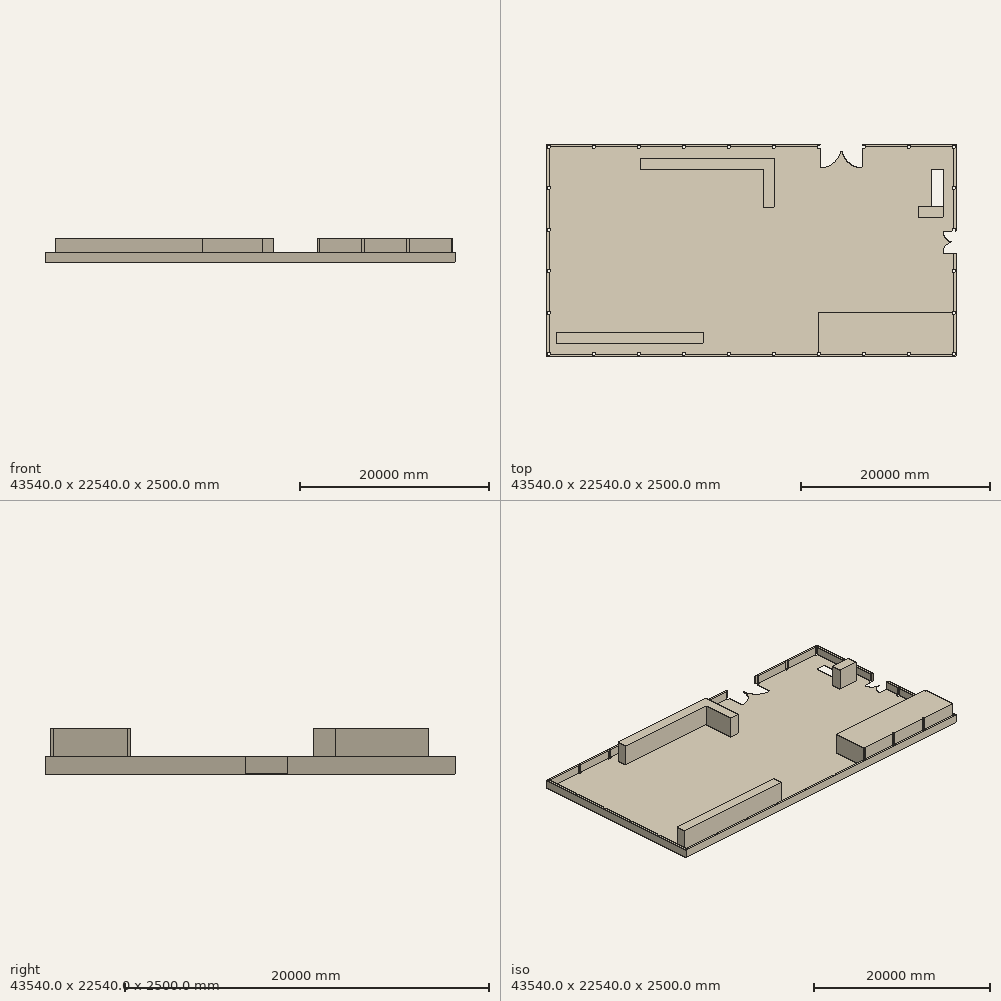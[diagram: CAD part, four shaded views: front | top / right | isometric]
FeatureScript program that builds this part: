
annotation { "Feature Type Name" : "Feature", "Feature Type Description" : "" }
export const myFeature = defineFeature(function(context is Context, id is Id, definition is map)
    precondition{}
    {
        {
            var Q0;
            Q0=qCreatedBy(makeId("Top.planeOp"),FACE);
            var sketch = newSketch(context, id + "F0", { "sketchPlane" : qUnion([Q0])});
            skLineSegment(sketch, "E0", {"start": v(0, 22000) * mm, "end": v(43000, 22000) * mm});
            skLineSegment(sketch, "E1", {"start": v(43000, 22000) * mm, "end": v(43000, 4400) * mm});
            skLineSegment(sketch, "E2", {"start": v(0, 22000) * mm, "end": v(0, 0) * mm});
            skLineSegment(sketch, "E3", {"start": v(0, 0) * mm, "end": v(28666.67, 0) * mm});
            skLineSegment(sketch, "E4.bottom", {"start": v(170, 22170) * mm, "end": v(-170, 22170) * mm});
            skLineSegment(sketch, "E4.top", {"start": v(170, 21830) * mm, "end": v(-170, 21830) * mm});
            skLineSegment(sketch, "E4.left", {"start": v(170, 22170) * mm, "end": v(170, 21830) * mm});
            skLineSegment(sketch, "E4.right", {"start": v(-170, 22170) * mm, "end": v(-170, 21830) * mm});
            skPoint(sketch, "E4.middle", {"position": v(0, 22000) * mm});
            skLineSegment(sketch, "E5.bottom", {"start": v(170, 170) * mm, "end": v(-170, 170) * mm});
            skLineSegment(sketch, "E5.top", {"start": v(170, -170) * mm, "end": v(-170, -170) * mm});
            skLineSegment(sketch, "E5.left", {"start": v(170, 170) * mm, "end": v(170, -170) * mm});
            skLineSegment(sketch, "E5.right", {"start": v(-170, 170) * mm, "end": v(-170, -170) * mm});
            skPoint(sketch, "E5.middle", {"position": v(0, 0) * mm});
            skLineSegment(sketch, "E6.0.1.0", {"start": v(170, 4230) * mm, "end": v(-170, 4230) * mm});
            skLineSegment(sketch, "E6.0.1.1", {"start": v(170, 4570) * mm, "end": v(-170, 4570) * mm});
            skLineSegment(sketch, "E6.0.1.2", {"start": v(170, 4570) * mm, "end": v(170, 4230) * mm});
            skLineSegment(sketch, "E6.0.1.3", {"start": v(-170, 4570) * mm, "end": v(-170, 4230) * mm});
            skLineSegment(sketch, "E6.0.2.0", {"start": v(170, 8630) * mm, "end": v(-170, 8630) * mm});
            skLineSegment(sketch, "E6.0.2.1", {"start": v(170, 8970) * mm, "end": v(-170, 8970) * mm});
            skLineSegment(sketch, "E6.0.2.2", {"start": v(170, 8970) * mm, "end": v(170, 8630) * mm});
            skLineSegment(sketch, "E6.0.2.3", {"start": v(-170, 8970) * mm, "end": v(-170, 8630) * mm});
            skLineSegment(sketch, "E6.0.3.0", {"start": v(170, 13030) * mm, "end": v(-170, 13030) * mm});
            skLineSegment(sketch, "E6.0.3.1", {"start": v(170, 13370) * mm, "end": v(-170, 13370) * mm});
            skLineSegment(sketch, "E6.0.3.2", {"start": v(170, 13370) * mm, "end": v(170, 13030) * mm});
            skLineSegment(sketch, "E6.0.3.3", {"start": v(-170, 13370) * mm, "end": v(-170, 13030) * mm});
            skLineSegment(sketch, "E6.0.4.0", {"start": v(170, 17430) * mm, "end": v(-170, 17430) * mm});
            skLineSegment(sketch, "E6.0.4.1", {"start": v(170, 17770) * mm, "end": v(-170, 17770) * mm});
            skLineSegment(sketch, "E6.0.4.2", {"start": v(170, 17770) * mm, "end": v(170, 17430) * mm});
            skLineSegment(sketch, "E6.0.4.3", {"start": v(-170, 17770) * mm, "end": v(-170, 17430) * mm});
            skLineSegment(sketch, "E7.0.1.0", {"start": v(43170, 4570) * mm, "end": v(43170, 4230) * mm});
            skPoint(sketch, "E7.0.1.1", {"position": v(43000, 4400) * mm});
            skLineSegment(sketch, "E7.0.1.2", {"start": v(42830, 4570) * mm, "end": v(42830, 4230) * mm});
            skLineSegment(sketch, "E7.0.1.4", {"start": v(43170, 4230) * mm, "end": v(42830, 4230) * mm});
            skLineSegment(sketch, "E7.0.1.5", {"start": v(43170, 4570) * mm, "end": v(42830, 4570) * mm});
            skLineSegment(sketch, "E7.0.2.0", {"start": v(43170, 8970) * mm, "end": v(43170, 8630) * mm});
            skPoint(sketch, "E7.0.2.1", {"position": v(43000, 8800) * mm});
            skLineSegment(sketch, "E7.0.2.2", {"start": v(42830, 8970) * mm, "end": v(42830, 8630) * mm});
            skLineSegment(sketch, "E7.0.2.4", {"start": v(43170, 8630) * mm, "end": v(42830, 8630) * mm});
            skLineSegment(sketch, "E7.0.2.5", {"start": v(43170, 8970) * mm, "end": v(42830, 8970) * mm});
            skLineSegment(sketch, "E7.0.3.0", {"start": v(43170, 13370) * mm, "end": v(43170, 13030) * mm});
            skPoint(sketch, "E7.0.3.1", {"position": v(43000, 13200) * mm});
            skLineSegment(sketch, "E7.0.3.2", {"start": v(42830, 13370) * mm, "end": v(42830, 13030) * mm});
            skLineSegment(sketch, "E7.0.3.4", {"start": v(43170, 13030) * mm, "end": v(42830, 13030) * mm});
            skLineSegment(sketch, "E7.0.3.5", {"start": v(43170, 13370) * mm, "end": v(42830, 13370) * mm});
            skLineSegment(sketch, "E7.0.4.0", {"start": v(43170, 17770) * mm, "end": v(43170, 17430) * mm});
            skPoint(sketch, "E7.0.4.1", {"position": v(43000, 17600) * mm});
            skLineSegment(sketch, "E7.0.4.2", {"start": v(42830, 17770) * mm, "end": v(42830, 17430) * mm});
            skLineSegment(sketch, "E7.0.4.4", {"start": v(43170, 17430) * mm, "end": v(42830, 17430) * mm});
            skLineSegment(sketch, "E7.0.4.5", {"start": v(43170, 17770) * mm, "end": v(42830, 17770) * mm});
            skPoint(sketch, "E8.1.0.0", {"position": v(4777.78, 22000) * mm});
            skLineSegment(sketch, "E8.1.0.1", {"start": v(4947.78, 22170) * mm, "end": v(4607.78, 22170) * mm});
            skLineSegment(sketch, "E8.1.0.2", {"start": v(4947.78, 22170) * mm, "end": v(4947.78, 21830) * mm});
            skLineSegment(sketch, "E8.1.0.3", {"start": v(4607.78, 22170) * mm, "end": v(4607.78, 21830) * mm});
            skLineSegment(sketch, "E8.1.0.4", {"start": v(4947.78, 21830) * mm, "end": v(4607.78, 21830) * mm});
            skPoint(sketch, "E8.2.0.0", {"position": v(9555.56, 22000) * mm});
            skLineSegment(sketch, "E8.2.0.1", {"start": v(9725.56, 22170) * mm, "end": v(9385.56, 22170) * mm});
            skLineSegment(sketch, "E8.2.0.2", {"start": v(9725.56, 22170) * mm, "end": v(9725.56, 21830) * mm});
            skLineSegment(sketch, "E8.2.0.3", {"start": v(9385.56, 22170) * mm, "end": v(9385.56, 21830) * mm});
            skLineSegment(sketch, "E8.2.0.4", {"start": v(9725.56, 21830) * mm, "end": v(9385.56, 21830) * mm});
            skPoint(sketch, "E8.3.0.0", {"position": v(14333.33, 22000) * mm});
            skLineSegment(sketch, "E8.3.0.1", {"start": v(14503.33, 22170) * mm, "end": v(14163.33, 22170) * mm});
            skLineSegment(sketch, "E8.3.0.2", {"start": v(14503.33, 22170) * mm, "end": v(14503.33, 21830) * mm});
            skLineSegment(sketch, "E8.3.0.3", {"start": v(14163.33, 22170) * mm, "end": v(14163.33, 21830) * mm});
            skLineSegment(sketch, "E8.3.0.4", {"start": v(14503.33, 21830) * mm, "end": v(14163.33, 21830) * mm});
            skPoint(sketch, "E8.4.0.0", {"position": v(19111.11, 22000) * mm});
            skLineSegment(sketch, "E8.4.0.1", {"start": v(19281.11, 22170) * mm, "end": v(18941.11, 22170) * mm});
            skLineSegment(sketch, "E8.4.0.2", {"start": v(19281.11, 22170) * mm, "end": v(19281.11, 21830) * mm});
            skLineSegment(sketch, "E8.4.0.3", {"start": v(18941.11, 22170) * mm, "end": v(18941.11, 21830) * mm});
            skLineSegment(sketch, "E8.4.0.4", {"start": v(19281.11, 21830) * mm, "end": v(18941.11, 21830) * mm});
            skPoint(sketch, "E8.5.0.0", {"position": v(23888.89, 22000) * mm});
            skLineSegment(sketch, "E8.5.0.1", {"start": v(24058.89, 22170) * mm, "end": v(23718.89, 22170) * mm});
            skLineSegment(sketch, "E8.5.0.2", {"start": v(24058.89, 22170) * mm, "end": v(24058.89, 21830) * mm});
            skLineSegment(sketch, "E8.5.0.3", {"start": v(23718.89, 22170) * mm, "end": v(23718.89, 21830) * mm});
            skLineSegment(sketch, "E8.5.0.4", {"start": v(24058.89, 21830) * mm, "end": v(23718.89, 21830) * mm});
            skPoint(sketch, "E8.6.0.0", {"position": v(28666.67, 22000) * mm});
            skLineSegment(sketch, "E8.6.0.1", {"start": v(28836.67, 22170) * mm, "end": v(28496.67, 22170) * mm});
            skLineSegment(sketch, "E8.6.0.2", {"start": v(28836.67, 22170) * mm, "end": v(28836.67, 21830) * mm});
            skLineSegment(sketch, "E8.6.0.3", {"start": v(28496.67, 22170) * mm, "end": v(28496.67, 21830) * mm});
            skLineSegment(sketch, "E8.6.0.4", {"start": v(28836.67, 21830) * mm, "end": v(28496.67, 21830) * mm});
            skPoint(sketch, "E8.7.0.0", {"position": v(33444.44, 22000) * mm});
            skLineSegment(sketch, "E8.7.0.1", {"start": v(33614.44, 22170) * mm, "end": v(33274.44, 22170) * mm});
            skLineSegment(sketch, "E8.7.0.2", {"start": v(33614.44, 22170) * mm, "end": v(33614.44, 21830) * mm});
            skLineSegment(sketch, "E8.7.0.3", {"start": v(33274.44, 22170) * mm, "end": v(33274.44, 21830) * mm});
            skLineSegment(sketch, "E8.7.0.4", {"start": v(33614.44, 21830) * mm, "end": v(33274.44, 21830) * mm});
            skPoint(sketch, "E8.8.0.0", {"position": v(38222.22, 22000) * mm});
            skLineSegment(sketch, "E8.8.0.1", {"start": v(38392.22, 22170) * mm, "end": v(38052.22, 22170) * mm});
            skLineSegment(sketch, "E8.8.0.2", {"start": v(38392.22, 22170) * mm, "end": v(38392.22, 21830) * mm});
            skLineSegment(sketch, "E8.8.0.3", {"start": v(38052.22, 22170) * mm, "end": v(38052.22, 21830) * mm});
            skLineSegment(sketch, "E8.8.0.4", {"start": v(38392.22, 21830) * mm, "end": v(38052.22, 21830) * mm});
            skPoint(sketch, "E8.9.0.0", {"position": v(43000, 22000) * mm});
            skLineSegment(sketch, "E8.9.0.1", {"start": v(43170, 22170) * mm, "end": v(42830, 22170) * mm});
            skLineSegment(sketch, "E8.9.0.2", {"start": v(43170, 22170) * mm, "end": v(43170, 21830) * mm});
            skLineSegment(sketch, "E8.9.0.3", {"start": v(42830, 22170) * mm, "end": v(42830, 21830) * mm});
            skLineSegment(sketch, "E8.9.0.4", {"start": v(43170, 21830) * mm, "end": v(42830, 21830) * mm});
            skLineSegment(sketch, "E9.1.0.0", {"start": v(4947.78, 170) * mm, "end": v(4607.78, 170) * mm});
            skLineSegment(sketch, "E9.1.0.1", {"start": v(4947.78, -170) * mm, "end": v(4607.78, -170) * mm});
            skPoint(sketch, "E9.1.0.2", {"position": v(4777.78, 0) * mm});
            skLineSegment(sketch, "E9.1.0.3", {"start": v(4607.78, 170) * mm, "end": v(4607.78, -170) * mm});
            skLineSegment(sketch, "E9.1.0.4", {"start": v(4947.78, 170) * mm, "end": v(4947.78, -170) * mm});
            skLineSegment(sketch, "E9.2.0.0", {"start": v(9725.56, 170) * mm, "end": v(9385.56, 170) * mm});
            skLineSegment(sketch, "E9.2.0.1", {"start": v(9725.56, -170) * mm, "end": v(9385.56, -170) * mm});
            skPoint(sketch, "E9.2.0.2", {"position": v(9555.56, 0) * mm});
            skLineSegment(sketch, "E9.2.0.3", {"start": v(9385.56, 170) * mm, "end": v(9385.56, -170) * mm});
            skLineSegment(sketch, "E9.2.0.4", {"start": v(9725.56, 170) * mm, "end": v(9725.56, -170) * mm});
            skLineSegment(sketch, "E9.3.0.0", {"start": v(14503.33, 170) * mm, "end": v(14163.33, 170) * mm});
            skLineSegment(sketch, "E9.3.0.1", {"start": v(14503.33, -170) * mm, "end": v(14163.33, -170) * mm});
            skPoint(sketch, "E9.3.0.2", {"position": v(14333.33, 0) * mm});
            skLineSegment(sketch, "E9.3.0.3", {"start": v(14163.33, 170) * mm, "end": v(14163.33, -170) * mm});
            skLineSegment(sketch, "E9.3.0.4", {"start": v(14503.33, 170) * mm, "end": v(14503.33, -170) * mm});
            skLineSegment(sketch, "E9.4.0.0", {"start": v(19281.11, 170) * mm, "end": v(18941.11, 170) * mm});
            skLineSegment(sketch, "E9.4.0.1", {"start": v(19281.11, -170) * mm, "end": v(18941.11, -170) * mm});
            skPoint(sketch, "E9.4.0.2", {"position": v(19111.11, 0) * mm});
            skLineSegment(sketch, "E9.4.0.3", {"start": v(18941.11, 170) * mm, "end": v(18941.11, -170) * mm});
            skLineSegment(sketch, "E9.4.0.4", {"start": v(19281.11, 170) * mm, "end": v(19281.11, -170) * mm});
            skLineSegment(sketch, "E9.5.0.0", {"start": v(24058.89, 170) * mm, "end": v(23718.89, 170) * mm});
            skLineSegment(sketch, "E9.5.0.1", {"start": v(24058.89, -170) * mm, "end": v(23718.89, -170) * mm});
            skPoint(sketch, "E9.5.0.2", {"position": v(23888.89, 0) * mm});
            skLineSegment(sketch, "E9.5.0.3", {"start": v(23718.89, 170) * mm, "end": v(23718.89, -170) * mm});
            skLineSegment(sketch, "E9.5.0.4", {"start": v(24058.89, 170) * mm, "end": v(24058.89, -170) * mm});
            skLineSegment(sketch, "E9.6.0.0", {"start": v(28836.67, 170) * mm, "end": v(28496.67, 170) * mm});
            skLineSegment(sketch, "E9.6.0.1", {"start": v(28836.67, -170) * mm, "end": v(28496.67, -170) * mm});
            skPoint(sketch, "E9.6.0.2", {"position": v(28666.67, 0) * mm});
            skLineSegment(sketch, "E9.6.0.3", {"start": v(28496.67, 170) * mm, "end": v(28496.67, -170) * mm});
            skLineSegment(sketch, "E9.6.0.4", {"start": v(28836.67, 170) * mm, "end": v(28836.67, -170) * mm});
            skLineSegment(sketch, "E9.7.0.0", {"start": v(33614.44, 170) * mm, "end": v(33274.44, 170) * mm});
            skLineSegment(sketch, "E9.7.0.1", {"start": v(33614.44, -170) * mm, "end": v(33274.44, -170) * mm});
            skPoint(sketch, "E9.7.0.2", {"position": v(33444.44, 0) * mm});
            skLineSegment(sketch, "E9.7.0.3", {"start": v(33274.44, 170) * mm, "end": v(33274.44, -170) * mm});
            skLineSegment(sketch, "E9.7.0.4", {"start": v(33614.44, 170) * mm, "end": v(33614.44, -170) * mm});
            skLineSegment(sketch, "E9.8.0.0", {"start": v(38392.22, 170) * mm, "end": v(38052.22, 170) * mm});
            skLineSegment(sketch, "E9.8.0.1", {"start": v(38392.22, -170) * mm, "end": v(38052.22, -170) * mm});
            skPoint(sketch, "E9.8.0.2", {"position": v(38222.22, 0) * mm});
            skLineSegment(sketch, "E9.8.0.3", {"start": v(38052.22, 170) * mm, "end": v(38052.22, -170) * mm});
            skLineSegment(sketch, "E9.8.0.4", {"start": v(38392.22, 170) * mm, "end": v(38392.22, -170) * mm});
            skLineSegment(sketch, "E9.9.0.0", {"start": v(43170, 170) * mm, "end": v(42830, 170) * mm});
            skLineSegment(sketch, "E9.9.0.1", {"start": v(43170, -170) * mm, "end": v(42830, -170) * mm});
            skPoint(sketch, "E9.9.0.2", {"position": v(43000, 0) * mm});
            skLineSegment(sketch, "E9.9.0.3", {"start": v(42830, 170) * mm, "end": v(42830, -170) * mm});
            skLineSegment(sketch, "E9.9.0.4", {"start": v(43170, 170) * mm, "end": v(43170, -170) * mm});
            skLineSegment(sketch, "E10.bottom", {"start": v(28836.67, 22000) * mm, "end": v(33274.44, 22000) * mm});
            skLineSegment(sketch, "E10.left", {"start": v(28836.67, 22000) * mm, "end": v(28836.67, 19781.11) * mm});
            skLineSegment(sketch, "E10.right", {"start": v(33274.44, 22000) * mm, "end": v(33274.44, 19781.11) * mm});
            skLineSegment(sketch, "E11", {"start": v(28666.67, 0) * mm, "end": v(43000, 0) * mm});
            skLineSegment(sketch, "E12", {"start": v(43000, 4400) * mm, "end": v(43000, 0) * mm});
            skLineSegment(sketch, "E13", {"start": v(43000, 4400) * mm, "end": v(28666.67, 4400) * mm});
            skLineSegment(sketch, "E14", {"start": v(28666.67, 4400) * mm, "end": v(28666.67, 0) * mm});
            skLineSegment(sketch, "E15", {"start": v(33444.44, 0) * mm, "end": v(33444.44, 4400) * mm});
            skLineSegment(sketch, "E16.top", {"start": v(43000, 10730) * mm, "end": v(41850, 10730) * mm});
            skLineSegment(sketch, "E16.left", {"start": v(43000, 13030) * mm, "end": v(43000, 10730) * mm});
            skLineSegment(sketch, "E17.top", {"start": v(69479.6, 14890.56) * mm, "end": v(70779.6, 14890.56) * mm});
            skLineSegment(sketch, "E17.left", {"start": v(69479.6, 17790.56) * mm, "end": v(69479.6, 14890.56) * mm});
            skLineSegment(sketch, "E17.right", {"start": v(70779.6, 17790.56) * mm, "end": v(70779.6, 14890.56) * mm});
            skLineSegment(sketch, "E18", {"start": v(69479.6, 17790.56) * mm, "end": v(69704.6, 17790.56) * mm});
            skLineSegment(sketch, "E19.MirrorCS", {"start": v(69904.6, 17790.56) * mm, "end": v(69904.6, 19390.56) * mm});
            skLineSegment(sketch, "E20", {"start": v(69704.6, 19390.56) * mm, "end": v(69704.6, 17790.56) * mm});
            skLineSegment(sketch, "E21.MirrorCS", {"start": v(70354.6, 17790.56) * mm, "end": v(70354.6, 19390.56) * mm});
            skLineSegment(sketch, "E22.MirrorCS", {"start": v(70554.6, 19390.56) * mm, "end": v(70554.6, 17790.56) * mm});
            skLineSegment(sketch, "E23", {"start": v(69704.6, 19390.56) * mm, "end": v(69904.6, 19390.56) * mm});
            skLineSegment(sketch, "E24.trimOffspring", {"start": v(70354.6, 19390.56) * mm, "end": v(70554.6, 19390.56) * mm});
            skLineSegment(sketch, "E25.bottom", {"start": v(64498.07, 14890.56) * mm, "end": v(65798.07, 14890.56) * mm});
            skLineSegment(sketch, "E25.top", {"start": v(64498.07, 19390.56) * mm, "end": v(65798.07, 19390.56) * mm});
            skLineSegment(sketch, "E25.left", {"start": v(64498.07, 14890.56) * mm, "end": v(64498.07, 19390.56) * mm});
            skLineSegment(sketch, "E25.right", {"start": v(65798.07, 14890.56) * mm, "end": v(65798.07, 19390.56) * mm});
            skLineSegment(sketch, "E26.trimOffspring", {"start": v(69904.6, 17790.56) * mm, "end": v(70354.6, 17790.56) * mm});
            skLineSegment(sketch, "E27.trimOffspring", {"start": v(70554.6, 17790.56) * mm, "end": v(70779.6, 17790.56) * mm});
            skLineSegment(sketch, "E28", {"start": v(30055.67, 19781.11) * mm, "end": v(30055.67, 12000) * mm});
            skLineSegment(sketch, "E29", {"start": v(30055.67, 12000) * mm, "end": v(0, 12000) * mm});
            skLineSegment(sketch, "E30", {"start": v(0, 10000) * mm, "end": v(32055.67, 10000) * mm});
            skLineSegment(sketch, "E31", {"start": v(32055.67, 10000) * mm, "end": v(32055.67, 19781.11) * mm});
            skLineSegment(sketch, "E32", {"start": v(31055.56, 19781.11) * mm, "end": v(31055.56, 11000) * mm, "construction": true});
            skLineSegment(sketch, "E33", {"start": v(31055.56, 11000) * mm, "end": v(0, 11000) * mm, "construction": true});
            skArc(sketch, "E34", {"start": v(43000, 11880) * mm, "mid": v(42186.83, 12216.83) * mm, "end": v(41850, 13030) * mm});
            skLineSegment(sketch, "E35", {"start": v(41850, 13030) * mm, "end": v(43000, 13030) * mm});
            skArc(sketch, "E36", {"start": v(43000, 11880) * mm, "mid": v(42186.83, 11543.17) * mm, "end": v(41850, 10730) * mm});
            skArc(sketch, "E37", {"start": v(31055.56, 22000) * mm, "mid": v(30405.66, 20431) * mm, "end": v(28836.67, 19781.11) * mm});
            skArc(sketch, "E38", {"start": v(31055.56, 22000) * mm, "mid": v(31705.45, 20431) * mm, "end": v(33274.44, 19781.11) * mm});
            skLineSegment(sketch, "E39", {"start": v(28836.67, 19781.11) * mm, "end": v(33274.44, 19781.11) * mm, "construction": true});
            skPoint(sketch, "E40", {"position": v(32055.67, 14890.56) * mm});
            skLineSegment(sketch, "E41", {"start": v(28666.67, 4400) * mm, "end": v(28666.67, 10000) * mm});
            skLineSegment(sketch, "E42.bottom", {"start": v(9758.5, 20769.78) * mm, "end": v(22758.5, 20769.78) * mm});
            skLineSegment(sketch, "E42.top", {"start": v(9758.5, 19549.78) * mm, "end": v(22758.5, 19549.78) * mm});
            skLineSegment(sketch, "E42.right", {"start": v(22758.5, 20769.78) * mm, "end": v(22758.5, 19549.78) * mm});
            skLineSegment(sketch, "E43.bottom", {"start": v(-270, 22270) * mm, "end": v(43270, 22270) * mm});
            skLineSegment(sketch, "E43.top", {"start": v(-270, -270) * mm, "end": v(43270, -270) * mm});
            skLineSegment(sketch, "E43.left", {"start": v(-270, 22270) * mm, "end": v(-270, -270) * mm});
            skLineSegment(sketch, "E43.right", {"start": v(43270, 22270) * mm, "end": v(43270, -270) * mm});
            skLineSegment(sketch, "E44", {"start": v(33274.44, 22170) * mm, "end": v(33274.44, 22270) * mm});
            skLineSegment(sketch, "E45", {"start": v(28836.67, 22170) * mm, "end": v(28836.67, 22270) * mm});
            skLineSegment(sketch, "E46", {"start": v(43170, 13030) * mm, "end": v(43270, 13030) * mm});
            skLineSegment(sketch, "E47", {"start": v(43000, 10730) * mm, "end": v(43270, 10730) * mm});
            skCircle(sketch, "E48", {"center": v(64985.2, 25566.08) * mm, "radius": 2342 * mm, "construction": true});
            skLineSegment(sketch, "E49", {"start": v(9758.5, 20769.78) * mm, "end": v(9758.5, 19549.78) * mm});
            skLineSegment(sketch, "E50.bottom", {"start": v(22758.5, 20769.78) * mm, "end": v(23978.5, 20769.78) * mm});
            skLineSegment(sketch, "E50.top", {"start": v(22758.5, 15569.78) * mm, "end": v(23978.5, 15569.78) * mm});
            skLineSegment(sketch, "E50.left", {"start": v(22758.5, 20769.78) * mm, "end": v(22758.5, 15569.78) * mm});
            skLineSegment(sketch, "E50.right", {"start": v(23978.5, 20769.78) * mm, "end": v(23978.5, 15569.78) * mm});
            skLineSegment(sketch, "E51.bottom", {"start": v(833.98, 2320.99) * mm, "end": v(16433.98, 2320.99) * mm});
            skLineSegment(sketch, "E51.top", {"start": v(833.98, 1100.99) * mm, "end": v(16433.98, 1100.99) * mm});
            skLineSegment(sketch, "E51.left", {"start": v(833.98, 2320.99) * mm, "end": v(833.98, 1100.99) * mm});
            skLineSegment(sketch, "E51.right", {"start": v(16433.98, 2320.99) * mm, "end": v(16433.98, 1100.99) * mm});
            skLineSegment(sketch, "E52.bottom", {"start": v(39250, 15695.4) * mm, "end": v(41850, 15695.4) * mm});
            skLineSegment(sketch, "E52.top", {"start": v(39250, 14475.4) * mm, "end": v(41850, 14475.4) * mm});
            skLineSegment(sketch, "E52.left", {"start": v(39250, 15695.4) * mm, "end": v(39250, 14475.4) * mm});
            skLineSegment(sketch, "E52.right", {"start": v(41850, 15695.4) * mm, "end": v(41850, 14475.4) * mm});
            skLineSegment(sketch, "E53.bottom", {"start": v(41850, 15695.4) * mm, "end": v(40630, 15695.4) * mm});
            skLineSegment(sketch, "E53.top", {"start": v(41850, 19595.4) * mm, "end": v(40630, 19595.4) * mm});
            skLineSegment(sketch, "E53.left", {"start": v(41850, 15695.4) * mm, "end": v(41850, 19595.4) * mm});
            skLineSegment(sketch, "E53.right", {"start": v(40630, 15695.4) * mm, "end": v(40630, 19595.4) * mm});
            skSolve(sketch);
        }
        {
            var Q0;
            {var subQ15=sQuery(id+"F0.wireOp",EDGE,"E6.0.1.2");Q0=makeQuery(id+"F0.imprint","IMPRINT",FACE,{"disambiguationData":[TD([[makeQuery(id+"F0.imprint","IMPRINT",EDGE,{"derivedFrom":subQ15}),1.0]])]});}
            var Q1;
            {var subQ82=sQuery(id+"F0.wireOp",EDGE,"E6.0.3.2");Q1=makeQuery(id+"F0.imprint","IMPRINT",FACE,{"disambiguationData":[TD([[makeQuery(id+"F0.imprint","IMPRINT",EDGE,{"derivedFrom":subQ82}),1.0]])]});}
            extrude(context, id + "F1", {"entities" : qUnion([Q0, Q1]), "depth" : 25 * mm, "offsetDistance" : 25 * mm});
        }
        {
            var Q0;
            {var subQ0=sQuery(id+"F0.wireOp",EDGE,"E42.bottom");Q0=makeQuery(id+"F0.imprint","IMPRINT",FACE,{"disambiguationData":[TD([[makeQuery(id+"F0.imprint","IMPRINT",EDGE,{"derivedFrom":subQ0}),-1.0]])]});}
            var Q1;
            {var subQ3=sQuery(id+"F0.wireOp",EDGE,"E50.bottom");Q1=makeQuery(id+"F0.imprint","IMPRINT",FACE,{"disambiguationData":[TD([[makeQuery(id+"F0.imprint","IMPRINT",EDGE,{"derivedFrom":subQ3}),-1.0]])]});}
            var Q2;
            Q2=makeQuery(id+"F0.imprint","IMPRINT",FACE,{"disambiguationData":[TD([[makeQuery(id+"F0.imprint","IMPRINT",EDGE,{"derivedFrom":sQuery(id+"F0.wireOp",EDGE,"E51.bottom")}),-1.0]])]});
            var Q3;
            Q3=makeQuery(id+"F0.imprint","IMPRINT",FACE,{"disambiguationData":[TD([[makeQuery(id+"F0.imprint","IMPRINT",EDGE,{"derivedFrom":sQuery(id+"F0.wireOp",EDGE,"E53.bottom")}),-1.0]])]});
            var Q4;
            Q4=makeQuery(id+"F0.imprint","IMPRINT",FACE,{"disambiguationData":[TD([[makeQuery(id+"F0.imprint","IMPRINT",EDGE,{"derivedFrom":sQuery(id+"F0.wireOp",EDGE,"E52.bottom")}),-1.0]])]});
            var Q5;
            {var subQ11=sQuery(id+"F0.wireOp",EDGE,"E9.8.0.0");Q5=makeQuery(id+"F0.imprint","IMPRINT",FACE,{"disambiguationData":[TD([[makeQuery(id+"F0.imprint","IMPRINT",EDGE,{"derivedFrom":subQ11}),-1.0]])]});}
            extrude(context, id + "F2", {"entities" : qUnion([Q0, Q1, Q2, Q3, Q4, Q5]), "depth" : 2500 * mm, "offsetDistance" : 25 * mm});
        }
        {
            var Q0;
            {var subQ7=sQuery(id+"F0.wireOp",EDGE,"E9.6.0.4");var subQ8=sQuery(id+"F0.wireOp",EDGE,"E9.6.0.0");var subQ9=makeQuery(id+"F0.imprint","INTERSECT",VERTEX,{"derivedFrom":[subQ8,subQ7]});Q0=makeQuery(id+"F0.imprint","IMPRINT",FACE,{"disambiguationData":[TD([[makeQuery(id+"F0.imprint","IMPRINT",EDGE,{"disambiguationData":[TD([[subQ9,-1.0]])],"derivedFrom":subQ8}),-1.0]])]});}
            extrude(context, id + "F3", {"entities" : qUnion([Q0]), "depth" : 2500 * mm, "offsetDistance" : 25 * mm});
        }
        {
            var Q0;
            {var subQ110=sQuery(id+"F0.wireOp",EDGE,"E4.bottom");Q0=makeQuery(id+"F0.imprint","IMPRINT",FACE,{"disambiguationData":[TD([[makeQuery(id+"F0.imprint","IMPRINT",EDGE,{"derivedFrom":subQ110}),-1.0]])]});}
            var Q1;
            {var subQ7=sQuery(id+"F0.wireOp",EDGE,"E7.0.3.0");Q1=makeQuery(id+"F0.imprint","IMPRINT",FACE,{"disambiguationData":[TD([[makeQuery(id+"F0.imprint","IMPRINT",EDGE,{"derivedFrom":subQ7}),1.0]])]});}
            extrude(context, id + "F4", {"entities" : qUnion([Q0, Q1]), "operationType" : NewBodyOperationType.ADD, "depth" : 1000 * mm, "offsetDistance" : 25 * mm});
        }
    });
